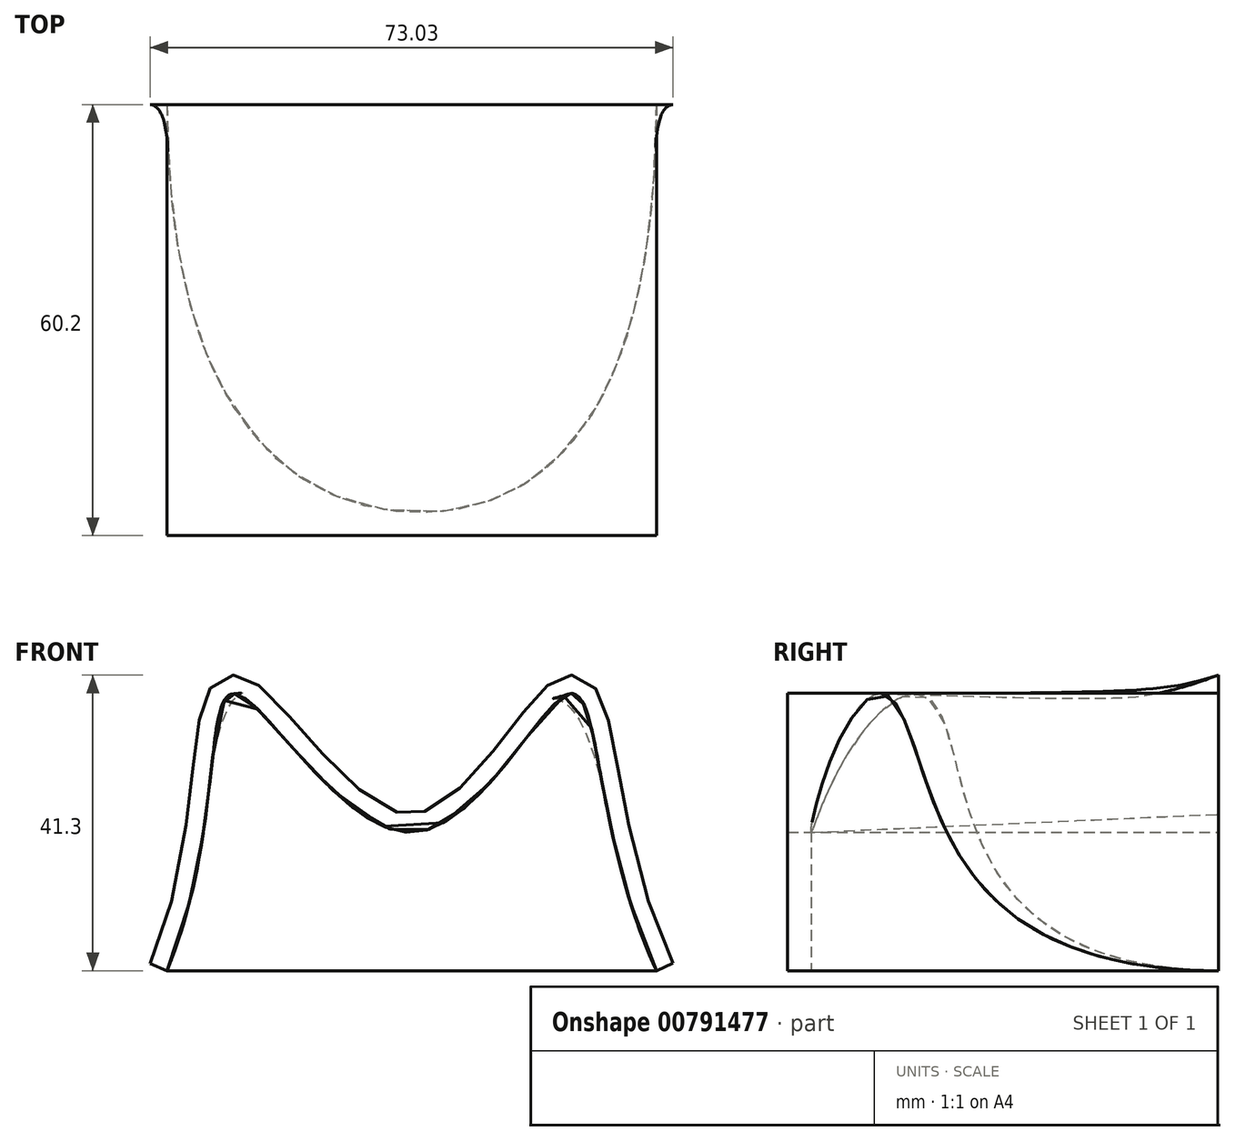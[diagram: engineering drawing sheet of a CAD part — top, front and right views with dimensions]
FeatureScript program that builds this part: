
annotation { "Feature Type Name" : "Feature", "Feature Type Description" : "" }
export const myFeature = defineFeature(function(context is Context, id is Id, definition is map)
    precondition{}
    {
        {
            var Q0;
            Q0=qCreatedBy(makeId("Top.planeOp"),FACE);
            var sketch = newSketch(context, id + "F0", { "sketchPlane" : qUnion([Q0])});
            skLineSegment(sketch, "E0.bottom", {"start": v(-34.19, 0) * mm, "end": v(34.19, 0) * mm, "construction": true});
            skLineSegment(sketch, "E0.top", {"start": v(-34.19, -56.9) * mm, "end": v(34.19, -56.9) * mm, "construction": true});
            skLineSegment(sketch, "E0.left", {"start": v(-34.19, 0) * mm, "end": v(-34.19, -56.9) * mm, "construction": true});
            skLineSegment(sketch, "E0.right", {"start": v(34.19, 0) * mm, "end": v(34.19, -56.9) * mm, "construction": true});
            skFitSpline(sketch, "E1", {"points": [v(-34.19, 0) * mm, v(0, -56.9) * mm, v(34.19, 0) * mm], "startDerivative": vector(0, -257.51) * mm, "endDerivative": vector(0, 272.72) * mm});
            skSolve(sketch);
        }
        {
            var Q0;
            Q0=qCreatedBy(makeId("Front.planeOp"),FACE);
            var sketch = newSketch(context, id + "F1", { "sketchPlane" : qUnion([Q0])});
            skLineSegment(sketch, "E2.bottom", {"start": v(-34.19, 0) * mm, "end": v(34.19, 0) * mm, "construction": true});
            skLineSegment(sketch, "E2.top", {"start": v(-34.19, 38.66) * mm, "end": v(34.19, 38.66) * mm, "construction": true});
            skLineSegment(sketch, "E2.left", {"start": v(-34.19, 0) * mm, "end": v(-34.19, 38.66) * mm, "construction": true});
            skLineSegment(sketch, "E2.right", {"start": v(34.19, 0) * mm, "end": v(34.19, 38.66) * mm, "construction": true});
            skFitSpline(sketch, "E3", {"points": [v(-34.19, 0) * mm, v(-24.43, 38.66) * mm, v(0, 19.33) * mm, v(21.82, 38.66) * mm, v(34.19, 0) * mm], "startDerivative": vector(90.36, 217.34) * mm, "endDerivative": vector(100.3, -215.4) * mm});
            skLineSegment(sketch, "E4", {"start": v(-34.19, 19.33) * mm, "end": v(34.19, 19.33) * mm, "construction": true});
            skSolve(sketch);
        }
        {
            var Q0;
            Q0 = qSketchRegion(id + "F0", true);
            var Q1;
            Q1=sQuery(id+"F1.wireOp",EDGE,"E3");
            extrude(context, id + "F2", {"entities" : qUnion([Q0]), "bodyType" : ToolBodyType.SURFACE, "surfaceEntities" : qUnion([Q1]), "depth" : 60.2 * mm, "offsetDistance" : 25.4 * mm});
        }
        {
            var Q0;
            Q0=sQuery(id+"F0.wireOp",EDGE,"E1");
            extrude(context, id + "F3", {"bodyType" : ToolBodyType.SURFACE, "surfaceEntities" : qUnion([Q0]), "endBound" : BoundingType.UP_TO_NEXT, "depth" : 25.4 * mm, "offsetDistance" : 25.4 * mm});
        }
        {
            var Q0;
            Q0=qCreatedBy(makeId("Front.planeOp"),FACE);
            var sketch = newSketch(context, id + "F4", { "sketchPlane" : qUnion([Q0])});
            skFitSpline(sketch, "E5.0", {"points": [v(-36.54, 0.98) * mm, v(-35.63, 3.14) * mm, v(-34.12, 7.54) * mm, v(-32.53, 14.06) * mm, v(-31.65, 19.27) * mm, v(-31.13, 23.18) * mm, v(-30.8, 25.97) * mm, v(-30.5, 28.58) * mm, v(-30.24, 30.98) * mm, v(-29.96, 33.17) * mm, v(-29.65, 35.13) * mm, v(-29.34, 36.58) * mm, v(-29.02, 37.65) * mm, v(-28.72, 38.41) * mm, v(-28.35, 39.16) * mm, v(-27.83, 39.89) * mm, v(-27.23, 40.47) * mm, v(-26.6, 40.85) * mm, v(-26.09, 41.07) * mm, v(-25.53, 41.22) * mm, v(-24.77, 41.3) * mm, v(-24.06, 41.2) * mm, v(-23.42, 41) * mm, v(-22.85, 40.77) * mm, v(-22.21, 40.42) * mm, v(-21.52, 39.92) * mm, v(-20.62, 39.18) * mm, v(-19.5, 38.11) * mm, v(-18.09, 36.62) * mm, v(-16.6, 34.95) * mm, v(-15.04, 33.17) * mm, v(-13.4, 31.33) * mm, v(-11.72, 29.49) * mm, v(-9.99, 27.71) * mm, v(-8.24, 26.06) * mm, v(-6.48, 24.61) * mm, v(-4.77, 23.41) * mm, v(-3.12, 22.53) * mm, v(-1.86, 22.09) * mm, v(-0.93, 21.9) * mm, v(-0.28, 21.85) * mm, v(0.35, 21.88) * mm, v(1, 22) * mm, v(1.69, 22.2) * mm, v(2.64, 22.57) * mm, v(3.9, 23.27) * mm, v(5.47, 24.43) * mm, v(7.07, 25.86) * mm, v(8.66, 27.5) * mm, v(10.21, 29.29) * mm, v(11.72, 31.14) * mm, v(13.18, 33) * mm, v(14.57, 34.82) * mm, v(15.9, 36.51) * mm, v(16.95, 37.78) * mm, v(17.78, 38.7) * mm, v(18.4, 39.33) * mm, v(19.03, 39.9) * mm, v(19.7, 40.42) * mm, v(20.34, 40.8) * mm, v(20.94, 41.05) * mm, v(21.43, 41.2) * mm, v(21.96, 41.29) * mm, v(22.52, 41.3) * mm, v(23.08, 41.23) * mm, v(23.81, 41.02) * mm, v(24.6, 40.59) * mm, v(25.3, 39.93) * mm, v(25.83, 39.24) * mm, v(26.24, 38.52) * mm, v(26.58, 37.77) * mm, v(26.97, 36.71) * mm, v(27.39, 35.27) * mm, v(27.84, 33.3) * mm, v(28.28, 31.1) * mm, v(28.73, 28.68) * mm, v(29.2, 26.06) * mm, v(29.74, 23.27) * mm, v(30.54, 19.34) * mm, v(31.76, 14.13) * mm, v(33.74, 7.6) * mm, v(35.49, 3.23) * mm, v(36.5, 1.07) * mm]});
            skLineSegment(sketch, "E6", {"start": v(-36.53, 0.98) * mm, "end": v(-34.19, 0) * mm});
            skLineSegment(sketch, "E7", {"start": v(36.5, 1.07) * mm, "end": v(34.19, 0) * mm});
            skSolve(sketch);
        }
        {
            var Q0;
            Q0=sQuery(id+"F4.wireOp",EDGE,"E5.0");
            var Q1;
            Q1=makeQuery(id+"F3.opExtrude","CAP_EDGE",EDGE,{"disambiguationData":[OSD([sQuery(id+"F0.wireOp",VERTEX,"E1.start")])],"isStart":false});
            loft(context, id + "F5", {"bodyType" : ToolBodyType.SURFACE, "wireProfilesArray" : [{ "wireProfileEntities" : qUnion([Q0]) }, { "wireProfileEntities" : qUnion([Q1]) }]});
        }
    });
